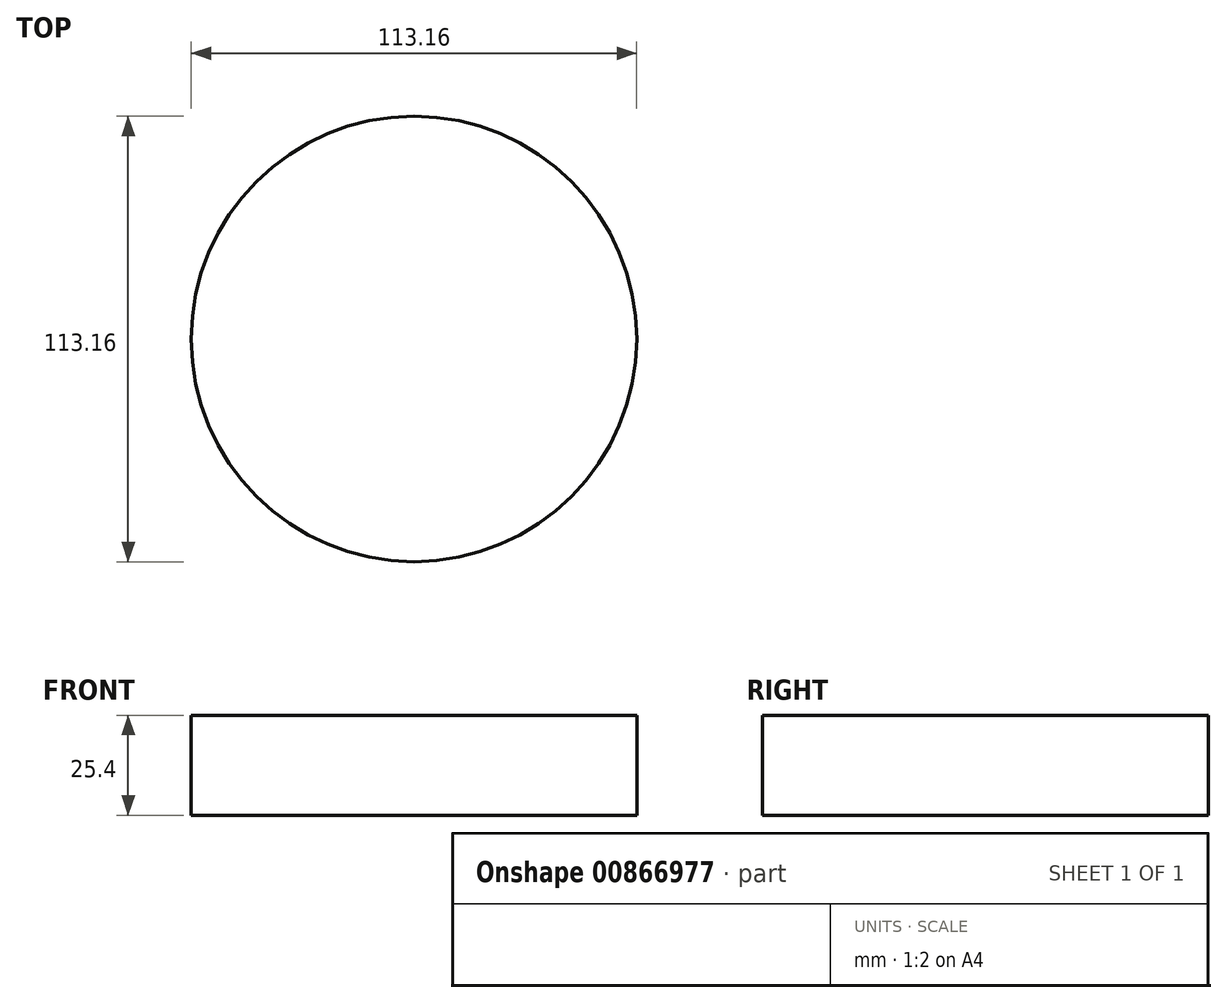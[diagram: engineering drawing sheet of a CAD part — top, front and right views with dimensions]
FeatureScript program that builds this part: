
annotation { "Feature Type Name" : "Feature", "Feature Type Description" : "" }
export const myFeature = defineFeature(function(context is Context, id is Id, definition is map)
    precondition{}
    {
        {
            var Q0;
            Q0=qCreatedBy(makeId("Top.planeOp"),FACE);
            var sketch = newSketch(context, id + "F0", { "sketchPlane" : qUnion([Q0])});
            skCircle(sketch, "E0", {"center": v(0, 0) * mm, "radius": 56.58 * mm});
            skSolve(sketch);
        }
        {
            var Q0;
            Q0=makeQuery(id+"F0.imprint","IMPRINT",FACE,{"disambiguationData":[TD([[makeQuery(id+"F0.imprint","IMPRINT",EDGE,{"derivedFrom":sQuery(id+"F0.wireOp",EDGE,"E0")}),1.0]])]});
            extrude(context, id + "F1", {"entities" : qUnion([Q0]), "depth" : 25.4 * mm, "offsetDistance" : 25.4 * mm});
        }
    });
